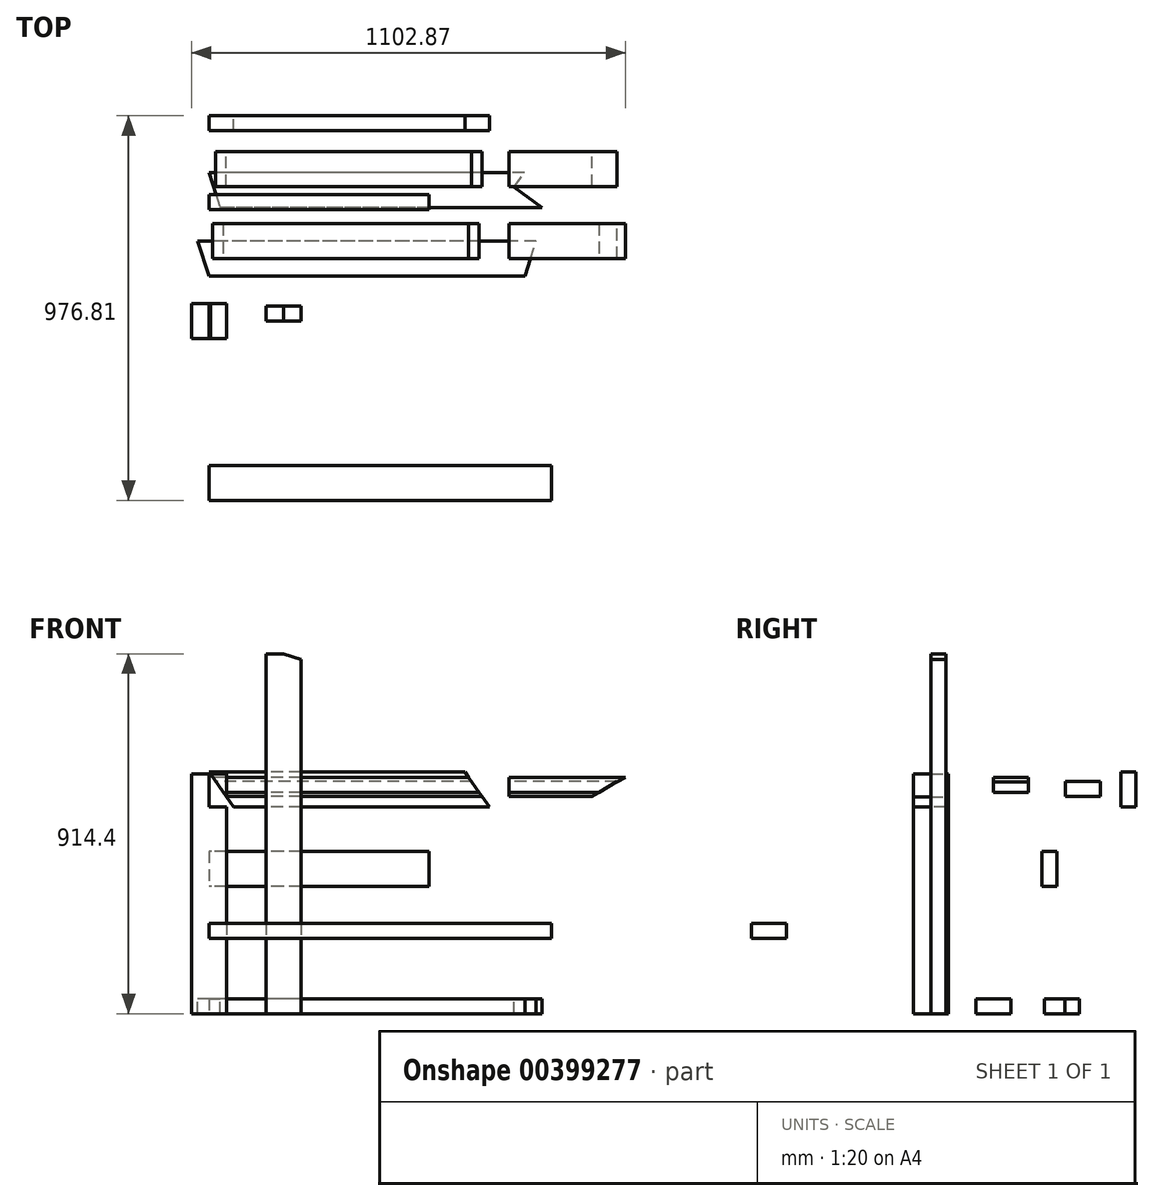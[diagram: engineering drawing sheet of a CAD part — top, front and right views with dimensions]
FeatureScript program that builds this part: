
annotation { "Feature Type Name" : "Feature", "Feature Type Description" : "" }
export const myFeature = defineFeature(function(context is Context, id is Id, definition is map)
    precondition{}
    {
        {
            var Q0;
            Q0=qCreatedBy(makeId("Top.planeOp"),FACE);
            var sketch = newSketch(context, id + "F0", { "sketchPlane" : qUnion([Q0])});
            skLineSegment(sketch, "E0.bottom", {"start": v(44.45, -44.45) * mm, "end": v(-44.45, -44.45) * mm});
            skLineSegment(sketch, "E0.top", {"start": v(44.45, 44.45) * mm, "end": v(-44.45, 44.45) * mm});
            skLineSegment(sketch, "E0.left", {"start": v(44.45, -44.45) * mm, "end": v(44.45, 44.45) * mm});
            skLineSegment(sketch, "E0.right", {"start": v(-44.45, -44.45) * mm, "end": v(-44.45, 44.45) * mm});
            skPoint(sketch, "E0.middle", {"position": v(0, 0) * mm});
            skSolve(sketch);
        }
        {
            var Q0;
            Q0=makeQuery(id+"F0.imprint","IMPRINT",FACE,{"disambiguationData":[TD([[makeQuery(id+"F0.imprint","IMPRINT",EDGE,{"derivedFrom":sQuery(id+"F0.wireOp",EDGE,"E0.bottom")}),-1.0]])]});
            extrude(context, id + "F1", {"entities" : qUnion([Q0]), "depth" : 609.6 * mm});
        }
        {
            var Q0;
            Q0=qCreatedBy(makeId("Top.planeOp"),FACE);
            var sketch = newSketch(context, id + "F2", { "sketchPlane" : qUnion([Q0])});
            skLineSegment(sketch, "E1.bottom", {"start": v(234, 0) * mm, "end": v(145.1, 0) * mm});
            skLineSegment(sketch, "E1.top", {"start": v(234, 38.1) * mm, "end": v(145.1, 38.1) * mm});
            skLineSegment(sketch, "E1.left", {"start": v(234, 0) * mm, "end": v(234, 38.1) * mm});
            skLineSegment(sketch, "E1.right", {"start": v(145.1, 0) * mm, "end": v(145.1, 38.1) * mm});
            skSolve(sketch);
        }
        {
            var Q0;
            Q0=makeQuery(id+"F2.imprint","IMPRINT",FACE,{"disambiguationData":[TD([[makeQuery(id+"F2.imprint","IMPRINT",EDGE,{"derivedFrom":sQuery(id+"F2.wireOp",EDGE,"E1.bottom")}),-1.0]])]});
            extrude(context, id + "F3", {"entities" : qUnion([Q0]), "depth" : 914.4 * mm});
        }
        {
            var Q0;
            Q0=makeQuery(id+"F3.opExtrude","SWEPT_FACE",FACE,{"disambiguationData":[OSD([sQuery(id+"F2.wireOp",EDGE,"E1.bottom")])]});
            var sketch = newSketch(context, id + "F4", { "sketchPlane" : qUnion([Q0])});
            skLineSegment(sketch, "E2", {"start": v(189.54, 914.4) * mm, "end": v(145.1, 899.96) * mm});
            skLineSegment(sketch, "E3", {"start": v(145.1, 899.96) * mm, "end": v(189.54, 914.4) * mm});
            skLineSegment(sketch, "E4", {"start": v(234, 899.96) * mm, "end": v(189.54, 914.4) * mm});
            skLineSegment(sketch, "E5", {"start": v(234, 899.96) * mm, "end": v(234, 914.4) * mm});
            skLineSegment(sketch, "E6", {"start": v(234, 914.4) * mm, "end": v(145.1, 914.4) * mm});
            skLineSegment(sketch, "E7", {"start": v(145.1, 914.4) * mm, "end": v(145.1, 899.96) * mm});
            skSolve(sketch);
        }
        {
            var Q0;
            {var subQ0=sQuery(id+"F4.wireOp",EDGE,"E3");Q0=makeQuery(id+"F4.imprint","IMPRINT",FACE,{"disambiguationData":[TD([[makeQuery(id+"F4.imprint","IMPRINT",EDGE,{"derivedFrom":subQ0}),1.0]])]});}
            var Q1;
            {var subQ0=sQuery(id+"F4.wireOp",EDGE,"E4");Q1=makeQuery(id+"F4.imprint","IMPRINT",FACE,{"disambiguationData":[TD([[makeQuery(id+"F4.imprint","IMPRINT",EDGE,{"derivedFrom":subQ0}),-1.0]])]});}
            extrude(context, id + "F5", {"entities" : qUnion([Q0, Q1]), "operationType" : NewBodyOperationType.REMOVE, "endBound" : BoundingType.THROUGH_ALL, "oppositeDirection" : true, "depth" : 25.4 * mm});
        }
        {
            var Q0;
            Q0=qCreatedBy(makeId("Right.planeOp"),FACE);
            var sketch = newSketch(context, id + "F6", { "sketchPlane" : qUnion([Q0])});
            skLineSegment(sketch, "E8.bottom", {"start": v(203.03, 0) * mm, "end": v(114.13, 0) * mm});
            skLineSegment(sketch, "E8.top", {"start": v(203.03, 38.1) * mm, "end": v(114.13, 38.1) * mm});
            skLineSegment(sketch, "E8.left", {"start": v(203.03, 0) * mm, "end": v(203.03, 38.1) * mm});
            skLineSegment(sketch, "E8.right", {"start": v(114.13, 0) * mm, "end": v(114.13, 38.1) * mm});
            skSolve(sketch);
        }
        {
            var Q0;
            Q0=makeQuery(id+"F6.imprint","IMPRINT",FACE,{"disambiguationData":[TD([[makeQuery(id+"F6.imprint","IMPRINT",EDGE,{"derivedFrom":sQuery(id+"F6.wireOp",EDGE,"E8.bottom")}),-1.0]])]});
            extrude(context, id + "F7", {"entities" : qUnion([Q0]), "depth" : 802.4 * mm});
        }
        {
            var Q0;
            Q0=makeQuery(id+"F7.opExtrude","SWEPT_FACE",FACE,{"disambiguationData":[OSD([sQuery(id+"F6.wireOp",EDGE,"E8.top")])]});
            var sketch = newSketch(context, id + "F8", { "sketchPlane" : qUnion([Q0])});
            skLineSegment(sketch, "E9", {"start": v(802.39, 114.13) * mm, "end": v(831.27, 203.03) * mm});
            skLineSegment(sketch, "E10", {"start": v(831.27, 203.03) * mm, "end": v(802.39, 203.03) * mm});
            skLineSegment(sketch, "E11", {"start": v(0, 114.13) * mm, "end": v(-28.89, 203.03) * mm});
            skLineSegment(sketch, "E12", {"start": v(0, 203.03) * mm, "end": v(-28.89, 203.03) * mm});
            skSolve(sketch);
        }
        {
            var Q0;
            Q0=makeQuery(id+"F8.imprint","IMPRINT",FACE,{"disambiguationData":[TD([[makeQuery(id+"F8.imprint","IMPRINT",EDGE,{"derivedFrom":sQuery(id+"F8.wireOp",EDGE,"E11")}),-1.0]])]});
            var Q1;
            Q1=makeQuery(id+"F8.imprint","IMPRINT",FACE,{"disambiguationData":[TD([[makeQuery(id+"F8.imprint","IMPRINT",EDGE,{"derivedFrom":sQuery(id+"F8.wireOp",EDGE,"E9")}),1.0]])]});
            extrude(context, id + "F9", {"entities" : qUnion([Q0, Q1]), "operationType" : NewBodyOperationType.ADD, "oppositeDirection" : true, "depth" : 38.1 * mm});
        }
        {
            var Q0;
            Q0=qCreatedBy(makeId("Right.planeOp"),FACE);
            var sketch = newSketch(context, id + "F10", { "sketchPlane" : qUnion([Q0])});
            skLineSegment(sketch, "E13.bottom", {"start": v(247.04, 562.74) * mm, "end": v(158.14, 562.74) * mm});
            skLineSegment(sketch, "E13.top", {"start": v(247.04, 600.84) * mm, "end": v(158.14, 600.84) * mm});
            skLineSegment(sketch, "E13.left", {"start": v(247.04, 562.74) * mm, "end": v(247.04, 600.84) * mm});
            skLineSegment(sketch, "E13.right", {"start": v(158.14, 562.74) * mm, "end": v(158.14, 600.84) * mm});
            skSolve(sketch);
        }
        {
            var Q0;
            Q0 = qSketchRegion(id + "F10", true);
            extrude(context, id + "F11", {"entities" : qUnion([Q0]), "depth" : 1058.42 * mm});
        }
        {
            var Q0;
            Q0=makeQuery(id+"F11.opExtrude","SWEPT_FACE",FACE,{"disambiguationData":[OSD([sQuery(id+"F10.wireOp",EDGE,"E13.right")])]});
            var sketch = newSketch(context, id + "F12", { "sketchPlane" : qUnion([Q0])});
            skLineSegment(sketch, "E14", {"start": v(1058.42, 600.84) * mm, "end": v(993.09, 562.74) * mm});
            skSolve(sketch);
        }
        {
            var Q0;
            {var subQ0=sQuery(id+"F12.wireOp",EDGE,"E14");Q0=makeQuery(id+"F12.imprint","IMPRINT",FACE,{"disambiguationData":[TD([[makeQuery(id+"F12.imprint","IMPRINT",EDGE,{"derivedFrom":subQ0}),1.0]])]});}
            extrude(context, id + "F13", {"entities" : qUnion([Q0]), "operationType" : NewBodyOperationType.REMOVE, "endBound" : BoundingType.THROUGH_ALL, "oppositeDirection" : true, "depth" : 25.4 * mm});
        }
        {
            var Q0;
            Q0=makeQuery(id+"F11.opExtrude","SWEPT_FACE",FACE,{"disambiguationData":[OSD([sQuery(id+"F10.wireOp",EDGE,"E13.left")])]});
            var sketch = newSketch(context, id + "F14", { "sketchPlane" : qUnion([Q0])});
            skLineSegment(sketch, "E15", {"start": v(0, 600.84) * mm, "end": v(-22.22, 562.74) * mm});
            skSolve(sketch);
        }
        {
            var Q0;
            {var subQ0=sQuery(id+"F14.wireOp",EDGE,"E15");Q0=makeQuery(id+"F14.imprint","IMPRINT",FACE,{"disambiguationData":[TD([[makeQuery(id+"F14.imprint","IMPRINT",EDGE,{"derivedFrom":subQ0}),1.0]])]});}
            extrude(context, id + "F15", {"entities" : qUnion([Q0]), "operationType" : NewBodyOperationType.REMOVE, "endBound" : BoundingType.THROUGH_ALL, "oppositeDirection" : true, "depth" : 25.4 * mm});
        }
        {
            var Q0;
            Q0=qCreatedBy(makeId("Right.planeOp"),FACE);
            var sketch = newSketch(context, id + "F16", { "sketchPlane" : qUnion([Q0])});
            skLineSegment(sketch, "E16.bottom", {"start": v(-455.9, 191.88) * mm, "end": v(-367, 191.88) * mm});
            skLineSegment(sketch, "E16.top", {"start": v(-455.9, 229.98) * mm, "end": v(-367, 229.98) * mm});
            skLineSegment(sketch, "E16.left", {"start": v(-455.9, 191.88) * mm, "end": v(-455.9, 229.98) * mm});
            skLineSegment(sketch, "E16.right", {"start": v(-367, 191.88) * mm, "end": v(-367, 229.98) * mm});
            skSolve(sketch);
        }
        {
            var Q0;
            Q0=makeQuery(id+"F16.imprint","IMPRINT",FACE,{"disambiguationData":[TD([[makeQuery(id+"F16.imprint","IMPRINT",EDGE,{"derivedFrom":sQuery(id+"F16.wireOp",EDGE,"E16.bottom")}),1.0]])]});
            extrude(context, id + "F17", {"entities" : qUnion([Q0]), "depth" : 869.95 * mm});
        }
        {
            var Q0;
            Q0=qCreatedBy(makeId("Right.planeOp"),FACE);
            var sketch = newSketch(context, id + "F18", { "sketchPlane" : qUnion([Q0])});
            skLineSegment(sketch, "E17.bottom", {"start": v(341.6, 590.35) * mm, "end": v(430.5, 590.35) * mm});
            skLineSegment(sketch, "E17.top", {"start": v(341.6, 552.25) * mm, "end": v(430.5, 552.25) * mm});
            skLineSegment(sketch, "E17.left", {"start": v(341.6, 590.35) * mm, "end": v(341.6, 552.25) * mm});
            skLineSegment(sketch, "E17.right", {"start": v(430.5, 590.35) * mm, "end": v(430.5, 552.25) * mm});
            skSolve(sketch);
        }
        {
            var Q0;
            Q0 = qSketchRegion(id + "F18", true);
            extrude(context, id + "F19", {"entities" : qUnion([Q0]), "depth" : 1036.83 * mm});
        }
        {
            var Q0;
            Q0=makeQuery(id+"F19.opExtrude","SWEPT_FACE",FACE,{"disambiguationData":[OSD([sQuery(id+"F18.wireOp",EDGE,"E17.right")])]});
            var sketch = newSketch(context, id + "F20", { "sketchPlane" : qUnion([Q0])});
            skLineSegment(sketch, "E18", {"start": v(-1036.83, 590.35) * mm, "end": v(-973.32, 552.25) * mm});
            skLineSegment(sketch, "E19", {"start": v(-22.86, 552.25) * mm, "end": v(0, 590.35) * mm});
            skSolve(sketch);
        }
        {
            var Q0;
            {var subQ0=sQuery(id+"F20.wireOp",EDGE,"E19");Q0=makeQuery(id+"F20.imprint","IMPRINT",FACE,{"disambiguationData":[TD([[makeQuery(id+"F20.imprint","IMPRINT",EDGE,{"derivedFrom":subQ0}),-1.0]])]});}
            extrude(context, id + "F21", {"entities" : qUnion([Q0]), "operationType" : NewBodyOperationType.REMOVE, "endBound" : BoundingType.THROUGH_ALL, "oppositeDirection" : true, "depth" : 25.4 * mm});
        }
        {
            var Q0;
            {var subQ0=sQuery(id+"F20.wireOp",EDGE,"E18");Q0=makeQuery(id+"F20.imprint","IMPRINT",FACE,{"disambiguationData":[TD([[makeQuery(id+"F20.imprint","IMPRINT",EDGE,{"derivedFrom":subQ0}),-1.0]])]});}
            extrude(context, id + "F22", {"entities" : qUnion([Q0]), "operationType" : NewBodyOperationType.REMOVE, "endBound" : BoundingType.THROUGH_ALL, "oppositeDirection" : true, "depth" : 25.4 * mm});
        }
        {
            var Q0;
            Q0=qCreatedBy(makeId("Right.planeOp"),FACE);
            var sketch = newSketch(context, id + "F23", { "sketchPlane" : qUnion([Q0])});
            skLineSegment(sketch, "E20.bottom", {"start": v(287.62, 38.1) * mm, "end": v(376.52, 38.1) * mm});
            skLineSegment(sketch, "E20.top", {"start": v(287.62, 0) * mm, "end": v(376.52, 0) * mm});
            skLineSegment(sketch, "E20.left", {"start": v(287.62, 38.1) * mm, "end": v(287.62, 0) * mm});
            skLineSegment(sketch, "E20.right", {"start": v(376.52, 38.1) * mm, "end": v(376.52, 0) * mm});
            skSolve(sketch);
        }
        {
            var Q0;
            Q0 = qSketchRegion(id + "F23", true);
            extrude(context, id + "F24", {"entities" : qUnion([Q0]), "depth" : 1066.8 * mm});
        }
        {
            var Q0;
            Q0=makeQuery(id+"F24.opExtrude","SWEPT_FACE",FACE,{"disambiguationData":[OSD([sQuery(id+"F23.wireOp",EDGE,"E20.bottom")])]});
            var sketch = newSketch(context, id + "F25", { "sketchPlane" : qUnion([Q0])});
            skLineSegment(sketch, "E21", {"start": v(0, 376.52) * mm, "end": v(28.89, 287.62) * mm});
            skSolve(sketch);
        }
        {
            var Q0;
            {var subQ0=sQuery(id+"F25.wireOp",EDGE,"E21");Q0=makeQuery(id+"F25.imprint","IMPRINT",FACE,{"disambiguationData":[TD([[makeQuery(id+"F25.imprint","IMPRINT",EDGE,{"derivedFrom":subQ0}),-1.0]])]});}
            extrude(context, id + "F26", {"entities" : qUnion([Q0]), "operationType" : NewBodyOperationType.REMOVE, "endBound" : BoundingType.THROUGH_ALL, "oppositeDirection" : true, "depth" : 25.4 * mm});
        }
        {
            var Q0;
            Q0=makeQuery(id+"F24.opExtrude","SWEPT_FACE",FACE,{"disambiguationData":[OSD([sQuery(id+"F23.wireOp",EDGE,"E20.bottom")])]});
            var sketch = newSketch(context, id + "F27", { "sketchPlane" : qUnion([Q0])});
            skLineSegment(sketch, "E22", {"start": v(846.77, 287.62) * mm, "end": v(774.84, 339.87) * mm});
            skLineSegment(sketch, "E23", {"start": v(774.84, 339.87) * mm, "end": v(801.47, 376.52) * mm});
            skSolve(sketch);
        }
        {
            var Q0;
            {var subQ4=sQuery(id+"F27.wireOp",EDGE,"E22");Q0=makeQuery(id+"F27.imprint","IMPRINT",FACE,{"disambiguationData":[TD([[makeQuery(id+"F27.imprint","IMPRINT",EDGE,{"derivedFrom":subQ4}),-1.0]])]});}
            extrude(context, id + "F28", {"entities" : qUnion([Q0]), "operationType" : NewBodyOperationType.REMOVE, "endBound" : BoundingType.THROUGH_ALL, "oppositeDirection" : true, "depth" : 25.4 * mm});
        }
        {
            var Q0;
            Q0=qCreatedBy(makeId("Right.planeOp"),FACE);
            var sketch = newSketch(context, id + "F29", { "sketchPlane" : qUnion([Q0])});
            skLineSegment(sketch, "E24.bottom", {"start": v(282.4, 412.86) * mm, "end": v(320.5, 412.86) * mm});
            skLineSegment(sketch, "E24.top", {"start": v(282.4, 323.96) * mm, "end": v(320.5, 323.96) * mm});
            skLineSegment(sketch, "E24.left", {"start": v(282.4, 412.86) * mm, "end": v(282.4, 323.96) * mm});
            skLineSegment(sketch, "E24.right", {"start": v(320.5, 412.86) * mm, "end": v(320.5, 323.96) * mm});
            skSolve(sketch);
        }
        {
            var Q0;
            Q0 = qSketchRegion(id + "F29", true);
            extrude(context, id + "F30", {"entities" : qUnion([Q0]), "depth" : 558.8 * mm});
        }
        {
            var Q0;
            Q0=qCreatedBy(makeId("Right.planeOp"),FACE);
            var sketch = newSketch(context, id + "F31", { "sketchPlane" : qUnion([Q0])});
            skLineSegment(sketch, "E25.bottom", {"start": v(482.8, 614.75) * mm, "end": v(520.9, 614.75) * mm});
            skLineSegment(sketch, "E25.top", {"start": v(482.8, 525.85) * mm, "end": v(520.9, 525.85) * mm});
            skLineSegment(sketch, "E25.left", {"start": v(482.8, 614.75) * mm, "end": v(482.8, 525.85) * mm});
            skLineSegment(sketch, "E25.right", {"start": v(520.9, 614.75) * mm, "end": v(520.9, 525.85) * mm});
            skSolve(sketch);
        }
        {
            var Q0;
            Q0=makeQuery(id+"F31.imprint","IMPRINT",FACE,{"disambiguationData":[TD([[makeQuery(id+"F31.imprint","IMPRINT",EDGE,{"derivedFrom":sQuery(id+"F31.wireOp",EDGE,"E25.bottom")}),-1.0]])]});
            extrude(context, id + "F32", {"entities" : qUnion([Q0]), "depth" : 762 * mm});
        }
        {
            var Q0;
            Q0=makeQuery(id+"F32.opExtrude","SWEPT_FACE",FACE,{"disambiguationData":[OSD([sQuery(id+"F31.wireOp",EDGE,"E25.right")])]});
            var sketch = newSketch(context, id + "F33", { "sketchPlane" : qUnion([Q0])});
            skLineSegment(sketch, "E26", {"start": v(0, 614.75) * mm, "end": v(-62.25, 525.85) * mm});
            skSolve(sketch);
        }
        {
            var Q0;
            {var subQ0=sQuery(id+"F33.wireOp",EDGE,"E26");Q0=makeQuery(id+"F33.imprint","IMPRINT",FACE,{"disambiguationData":[TD([[makeQuery(id+"F33.imprint","IMPRINT",EDGE,{"derivedFrom":subQ0}),1.0]])]});}
            extrude(context, id + "F34", {"entities" : qUnion([Q0]), "operationType" : NewBodyOperationType.REMOVE, "endBound" : BoundingType.THROUGH_ALL, "oppositeDirection" : true, "depth" : 25.4 * mm});
        }
        {
            var Q0;
            Q0=makeQuery(id+"F32.opExtrude","SWEPT_FACE",FACE,{"disambiguationData":[OSD([sQuery(id+"F31.wireOp",EDGE,"E25.right")])]});
            var sketch = newSketch(context, id + "F35", { "sketchPlane" : qUnion([Q0])});
            skLineSegment(sketch, "E27", {"start": v(-712.49, 525.85) * mm, "end": v(-650.24, 614.75) * mm});
            skSolve(sketch);
        }
        {
            var Q0;
            {var subQ0=sQuery(id+"F35.wireOp",EDGE,"E27");Q0=makeQuery(id+"F35.imprint","IMPRINT",FACE,{"disambiguationData":[TD([[makeQuery(id+"F35.imprint","IMPRINT",EDGE,{"derivedFrom":subQ0}),1.0]])]});}
            extrude(context, id + "F36", {"entities" : qUnion([Q0]), "operationType" : NewBodyOperationType.REMOVE, "endBound" : BoundingType.THROUGH_ALL, "oppositeDirection" : true, "depth" : 25.4 * mm});
        }
        {
            var Q0;
            Q0=makeQuery(id+"F26.boolean.opBoolean","COPY",FACE,{"derivedFrom":makeQuery(id+"F26.opExtrude","SWEPT_FACE",FACE,{"disambiguationData":[OSD([sQuery(id+"F25.wireOp",EDGE,"E21")])]})});
            var sketch = newSketch(context, id + "F37", { "sketchPlane" : qUnion([Q0])});
            skLineSegment(sketch, "E28.bottom", {"start": v(-992.76, 0) * mm, "end": v(-1081.66, 0) * mm});
            skLineSegment(sketch, "E28.top", {"start": v(-992.76, 38.1) * mm, "end": v(-1081.66, 38.1) * mm});
            skLineSegment(sketch, "E28.left", {"start": v(-992.76, 0) * mm, "end": v(-992.76, 38.1) * mm});
            skLineSegment(sketch, "E28.right", {"start": v(-1081.66, 0) * mm, "end": v(-1081.66, 38.1) * mm});
            skSolve(sketch);
        }
        {
            var Q0;
            Q0=makeQuery(id+"F37.imprint","IMPRINT",FACE,{"disambiguationData":[TD([[makeQuery(id+"F37.imprint","IMPRINT",EDGE,{"derivedFrom":sQuery(id+"F37.wireOp",EDGE,"E28.bottom")}),-1.0]])]});
            extrude(context, id + "F38", {"entities" : qUnion([Q0]), "depth" : 508 * mm});
        }
        {
            var Q0;
            Q0=makeQuery(id+"F38.opExtrude","SWEPT_FACE",FACE,{"disambiguationData":[OSD([sQuery(id+"F37.wireOp",EDGE,"E28.top")])]});
            var sketch = newSketch(context, id + "F39", { "sketchPlane" : qUnion([Q0])});
            skLineSegment(sketch, "E29", {"start": v(-706.73, 907.7) * mm, "end": v(-630.45, 839) * mm});
            skSolve(sketch);
        }
        {
            var Q0;
            {var subQ0=sQuery(id+"F39.wireOp",EDGE,"E29");Q0=makeQuery(id+"F39.imprint","IMPRINT",FACE,{"disambiguationData":[TD([[makeQuery(id+"F39.imprint","IMPRINT",EDGE,{"derivedFrom":subQ0}),-1.0]])]});}
            extrude(context, id + "F40", {"entities" : qUnion([Q0]), "operationType" : NewBodyOperationType.REMOVE, "endBound" : BoundingType.THROUGH_ALL, "oppositeDirection" : true, "depth" : 25.4 * mm});
        }
        {
            var Q0;
            Q0=makeQuery(id+"F38.opExtrude","SWEPT_FACE",FACE,{"disambiguationData":[OSD([sQuery(id+"F37.wireOp",EDGE,"E28.top")])]});
            var sketch = newSketch(context, id + "F41", { "sketchPlane" : qUnion([Q0])});
            skLineSegment(sketch, "E30", {"start": v(-223.6, 1064.67) * mm, "end": v(-244.94, 964.26) * mm});
            skSolve(sketch);
        }
        {
            var Q0;
            {var subQ0=sQuery(id+"F41.wireOp",EDGE,"E30");Q0=makeQuery(id+"F41.imprint","IMPRINT",FACE,{"disambiguationData":[TD([[makeQuery(id+"F41.imprint","IMPRINT",EDGE,{"derivedFrom":subQ0}),1.0]])]});}
            extrude(context, id + "F42", {"entities" : qUnion([Q0]), "operationType" : NewBodyOperationType.REMOVE, "endBound" : BoundingType.THROUGH_ALL, "oppositeDirection" : true, "depth" : 25.4 * mm});
        }
        {
            var Q0;
            Q0=makeQuery(id+"F38.opExtrude","SWEPT_BODY",BODY,{"disambiguationData":[OSD([sQuery(id+"F37.wireOp",EDGE,"E28.bottom"),sQuery(id+"F37.wireOp",EDGE,"E28.top"),sQuery(id+"F37.wireOp",EDGE,"E28.left"),sQuery(id+"F37.wireOp",EDGE,"E28.right")])]});
            deleteBodies(context, id + "F43", {"entities" : qUnion([Q0])});
        }
    });
